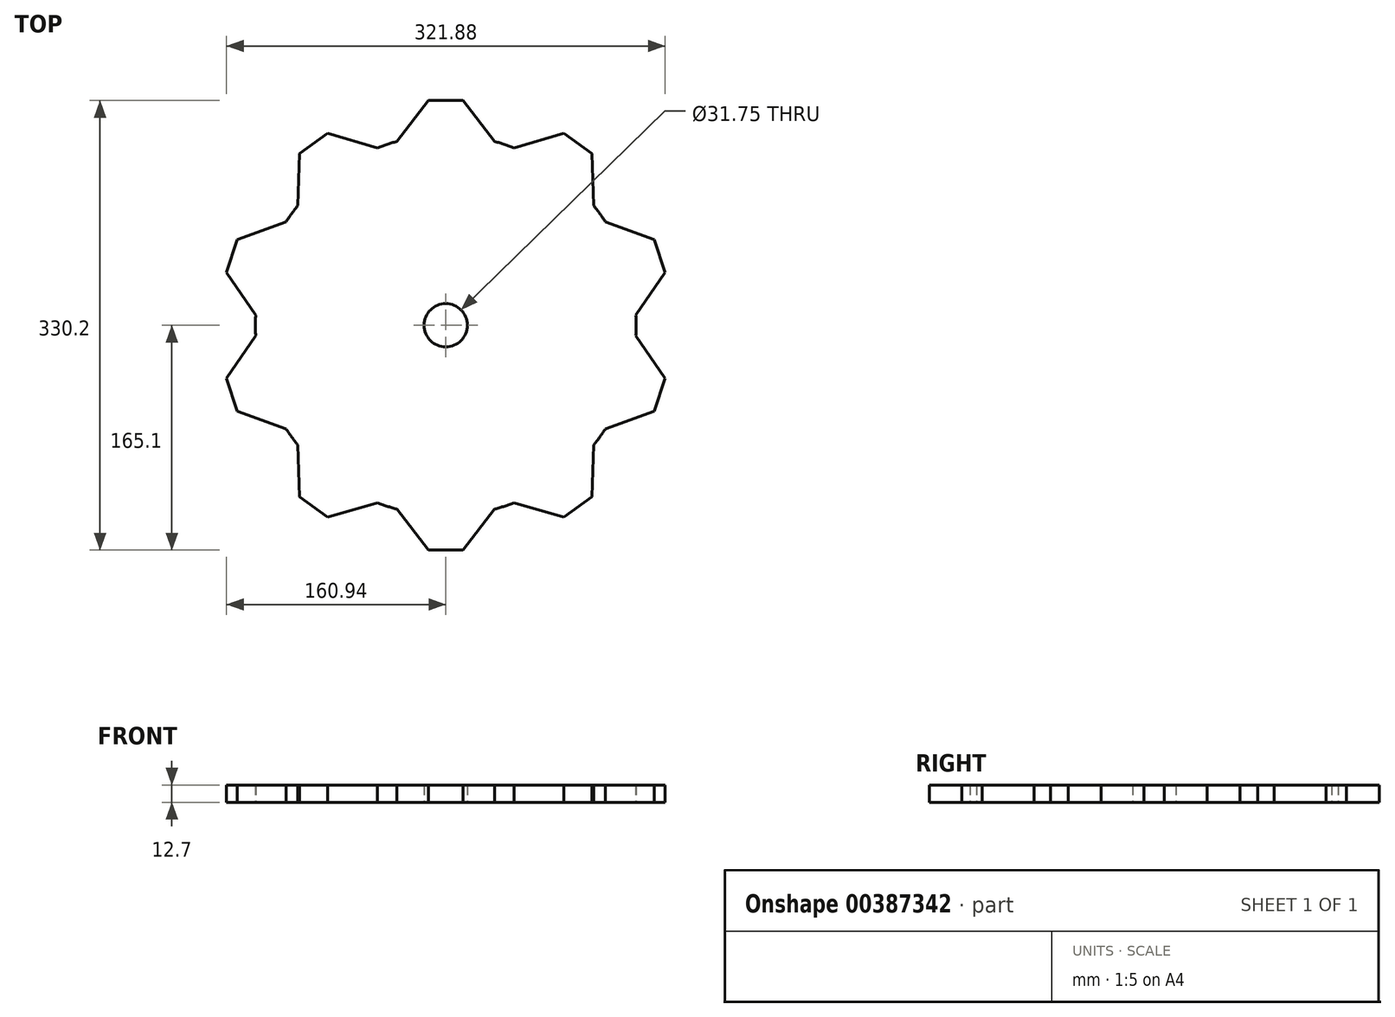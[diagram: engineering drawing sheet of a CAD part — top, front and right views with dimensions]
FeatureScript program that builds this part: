
annotation { "Feature Type Name" : "Feature", "Feature Type Description" : "" }
export const myFeature = defineFeature(function(context is Context, id is Id, definition is map)
    precondition{}
    {
        {
            var Q0;
            Q0=qCreatedBy(makeId("Top.planeOp"),FACE);
            var sketch = newSketch(context, id + "F0", { "sketchPlane" : qUnion([Q0])});
            skCircle(sketch, "E0", {"center": v(0, 0) * mm, "radius": 139.7 * mm});
            skLineSegment(sketch, "E1", {"start": v(0, 165.1) * mm, "end": v(12.7, 165.1) * mm});
            skLineSegment(sketch, "E2", {"start": v(12.7, 165.1) * mm, "end": v(0, 165.1) * mm});
            skLineSegment(sketch, "E3", {"start": v(0, 165.1) * mm, "end": v(-12.7, 165.1) * mm});
            skLineSegment(sketch, "E4", {"start": v(12.7, 165.1) * mm, "end": v(36.03, 134.97) * mm});
            skLineSegment(sketch, "E5", {"start": v(-12.7, 165.1) * mm, "end": v(-36.03, 134.97) * mm});
            skLineSegment(sketch, "E6.1.0", {"start": v(-107.32, 126.1) * mm, "end": v(-108.48, 88.02) * mm});
            skLineSegment(sketch, "E6.1.1", {"start": v(-86.77, 141.03) * mm, "end": v(-50.2, 130.37) * mm});
            skLineSegment(sketch, "E6.1.2", {"start": v(-86.77, 141.03) * mm, "end": v(-97.04, 133.57) * mm});
            skLineSegment(sketch, "E6.1.3", {"start": v(-97.04, 133.57) * mm, "end": v(-107.32, 126.1) * mm});
            skLineSegment(sketch, "E6.2.0", {"start": v(-160.94, 38.94) * mm, "end": v(-139.5, 7.45) * mm});
            skLineSegment(sketch, "E6.2.1", {"start": v(-153.1, 63.1) * mm, "end": v(-117.24, 75.97) * mm});
            skLineSegment(sketch, "E6.2.2", {"start": v(-153.1, 63.1) * mm, "end": v(-157.02, 51.02) * mm});
            skLineSegment(sketch, "E6.2.3", {"start": v(-157.02, 51.02) * mm, "end": v(-160.94, 38.94) * mm});
            skLineSegment(sketch, "E6.3.0", {"start": v(-153.1, -63.1) * mm, "end": v(-117.24, -75.97) * mm});
            skLineSegment(sketch, "E6.3.1", {"start": v(-160.94, -38.94) * mm, "end": v(-139.5, -7.45) * mm});
            skLineSegment(sketch, "E6.3.2", {"start": v(-160.94, -38.94) * mm, "end": v(-157.02, -51.02) * mm});
            skLineSegment(sketch, "E6.3.3", {"start": v(-157.02, -51.02) * mm, "end": v(-153.1, -63.1) * mm});
            skLineSegment(sketch, "E6.4.0", {"start": v(-86.77, -141.03) * mm, "end": v(-50.2, -130.37) * mm});
            skLineSegment(sketch, "E6.4.1", {"start": v(-107.32, -126.1) * mm, "end": v(-108.48, -88.02) * mm});
            skLineSegment(sketch, "E6.4.2", {"start": v(-107.32, -126.1) * mm, "end": v(-97.04, -133.57) * mm});
            skLineSegment(sketch, "E6.4.3", {"start": v(-97.04, -133.57) * mm, "end": v(-86.77, -141.03) * mm});
            skLineSegment(sketch, "E6.5.0", {"start": v(12.7, -165.1) * mm, "end": v(36.03, -134.97) * mm});
            skLineSegment(sketch, "E6.5.1", {"start": v(-12.7, -165.1) * mm, "end": v(-36.03, -134.97) * mm});
            skLineSegment(sketch, "E6.5.2", {"start": v(-12.7, -165.1) * mm, "end": v(0, -165.1) * mm});
            skLineSegment(sketch, "E6.5.3", {"start": v(0, -165.1) * mm, "end": v(12.7, -165.1) * mm});
            skLineSegment(sketch, "E6.6.0", {"start": v(107.32, -126.1) * mm, "end": v(108.48, -88.02) * mm});
            skLineSegment(sketch, "E6.6.1", {"start": v(86.77, -141.03) * mm, "end": v(50.2, -130.37) * mm});
            skLineSegment(sketch, "E6.6.2", {"start": v(86.77, -141.03) * mm, "end": v(97.04, -133.57) * mm});
            skLineSegment(sketch, "E6.6.3", {"start": v(97.04, -133.57) * mm, "end": v(107.32, -126.1) * mm});
            skLineSegment(sketch, "E6.7.0", {"start": v(160.94, -38.94) * mm, "end": v(139.5, -7.45) * mm});
            skLineSegment(sketch, "E6.7.1", {"start": v(153.1, -63.1) * mm, "end": v(117.24, -75.97) * mm});
            skLineSegment(sketch, "E6.7.2", {"start": v(153.1, -63.1) * mm, "end": v(157.02, -51.02) * mm});
            skLineSegment(sketch, "E6.7.3", {"start": v(157.02, -51.02) * mm, "end": v(160.94, -38.94) * mm});
            skLineSegment(sketch, "E6.8.0", {"start": v(153.1, 63.1) * mm, "end": v(117.24, 75.97) * mm});
            skLineSegment(sketch, "E6.8.1", {"start": v(160.94, 38.94) * mm, "end": v(139.5, 7.45) * mm});
            skLineSegment(sketch, "E6.8.2", {"start": v(160.94, 38.94) * mm, "end": v(157.02, 51.02) * mm});
            skLineSegment(sketch, "E6.8.3", {"start": v(157.02, 51.02) * mm, "end": v(153.1, 63.1) * mm});
            skLineSegment(sketch, "E6.9.0", {"start": v(86.77, 141.03) * mm, "end": v(50.2, 130.37) * mm});
            skLineSegment(sketch, "E6.9.1", {"start": v(107.32, 126.1) * mm, "end": v(108.48, 88.02) * mm});
            skLineSegment(sketch, "E6.9.2", {"start": v(107.32, 126.1) * mm, "end": v(97.04, 133.57) * mm});
            skLineSegment(sketch, "E6.9.3", {"start": v(97.04, 133.57) * mm, "end": v(86.77, 141.03) * mm});
            skCircle(sketch, "E7", {"center": v(0, 0) * mm, "radius": 15.88 * mm});
            skSolve(sketch);
        }
        {
            var Q0;
            Q0 = qSketchRegion(id + "F0", true);
            extrude(context, id + "F1", {"entities" : qUnion([Q0]), "depth" : 12.7 * mm});
        }
    });
